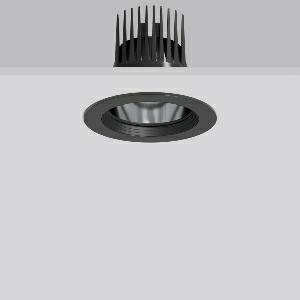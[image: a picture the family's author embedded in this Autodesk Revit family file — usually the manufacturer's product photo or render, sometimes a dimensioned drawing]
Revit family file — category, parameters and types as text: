
# Revit family: heledon_maxi_e_901764_003_3136
name_source: partatom
category: Lighting Fixtures
units: mm (PartAtom-declared; Revit-internal decimal feet)

## family parameters
Cut with Voids When Loaded = No
Host = Face
Light Source = No
Part Type = Normal
Room Calculation Point = No
Round Connector Dimension = Use Diameter
Shared = No

## types (1)
- HELEDON maxi E (1 x LED Modul 930, 4300 lm, 3000)
    Apparent Load = 35 VA
    Approval mark = CE
    CIE Flux Codes = 100 100 100 100 100
    Color Rendering = 90
    Color Temperature = 3000
    Default Elevation = 1800 mm
    Description = Series: HELEDON maxi
Round recessed downlight. Housing: die-cast aluminium, powder-coated. Black plastic ring and recessed LED to prevent glare from the side. Optical assembly with reflector made of MIRO-Silver with 98% total light reflection for outstanding efficiency - can be changed without tools. Best colour rendering index Ra>90. Suitable for Recessed ceiling mounting. Installation without tools thanks to spring fastening system. Including separate LED converter with connecting cable 600 mm.High quality converter without flickering and stroboscopic effect. Through-wiring box (5 pole) available as accessory. The following accessories can be mounted without use of tools: interchangeable lenses, decorative glasses, honeycomb louvre, clear and frosted diffusers, white interchangeable plastic ring. 
Colour: deep black, matt (RAL 9005)
Diameter: 162 mm
Height: 3 mm
Cut-out diameter: 152 mm
Recess height: 200 mm
Luminaire: recess height: 135 mm
Lamp: LED
Socket: without socket
Colour temperature: 3000K
Colour rendering index (CRI): 92
System power: 35 W
Rated luminous flux: 4300 lm
Luminous efficiency: 123 lm/W
Control gear: Regulated power supply
Protection class: II
Type of protection: IP 20
    Height = 0 mm  [stored 0 ft]
    Lamp = 1 x LED Modul 930
    Lamp Light Flux = 4300 lm
    Lamp count = 1
    Length = 162 mm
    Lifetime = 50000 h
    Luminous efficacy = 123 lm/W
    Manufacturer = RZB
    ModVariant = No
    Model = 901764.003
    Mounting Place = Ceiling
    Mounting Type = Recessed
    Number of Poles = 1
    OnlyDefault = Yes
    Power Factor = 1
    Product Name = HELEDON maxi E
    Product group = Recessed downlights
    ProductGroupID = 402
    Protection Class = Protection class II
    Protection Degree = IP 20
    RLX_Detail_Level = 1
    RLX_Emergency_Light_Flux = 0 lm
    RLX_Emergency_Type = 0
    RLX_Emergency_Type_DB = No
    RlxData = <blob elided: 122357 chars, md5=44c2b58c>
    Socket = socket
    Standby Power = 0 W
    System Light Flux = 4300 lm
    System Power = 35 W
    Type Comments = Product without accessories
    Type Image = 901662.003.jpg
    URL = http://relux.com
    VarID = ---
    Voltage = 230 V
    Voltage Range = 220-240 V
    Weight = 0.00 kg
    Width = 0 mm  [stored 0 ft]

note: [stored X ft] marks values corroborated as IEEE doubles in the binary element streams (Revit-internal decimal feet)

## geometry (parser evidence)
native form markers: Blend x4, Sweep x12
no freeform markers — native parametric forms only
